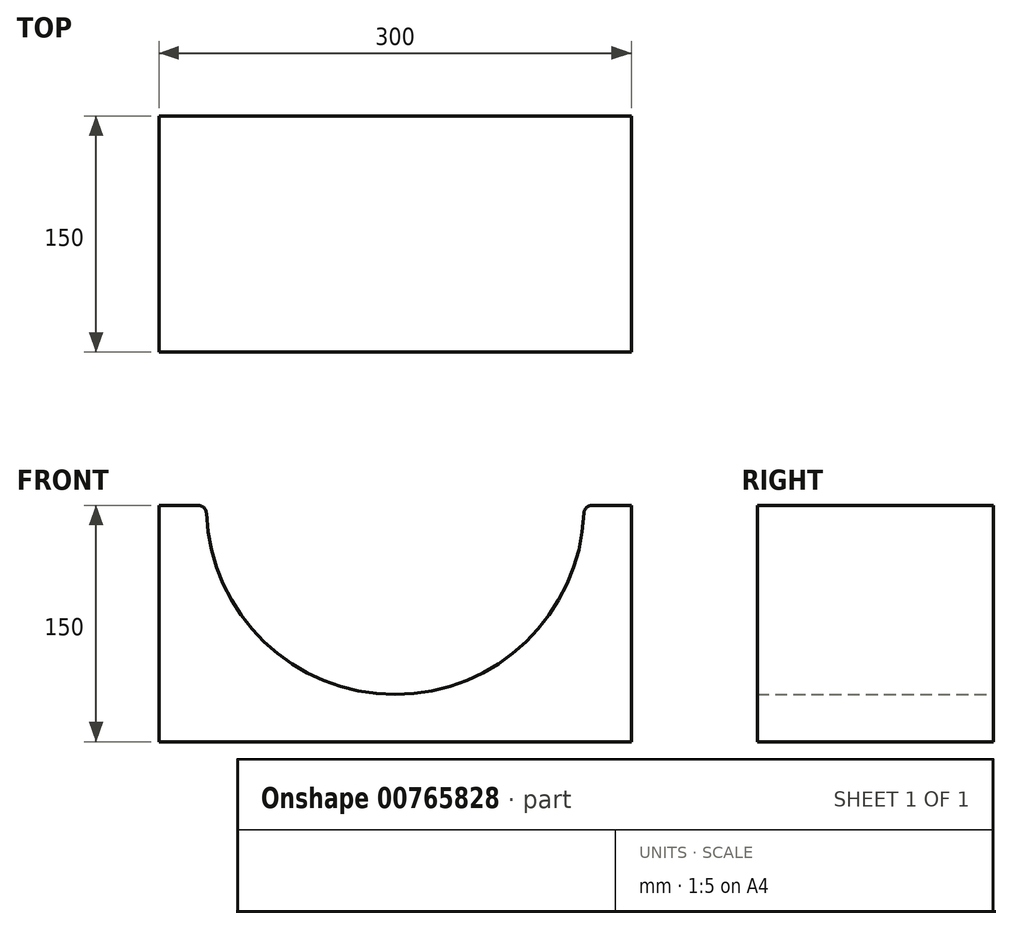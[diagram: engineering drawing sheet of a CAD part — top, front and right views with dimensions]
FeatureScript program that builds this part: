
annotation { "Feature Type Name" : "Feature", "Feature Type Description" : "" }
export const myFeature = defineFeature(function(context is Context, id is Id, definition is map)
    precondition{}
    {
        {
            var Q0;
            Q0=qCreatedBy(makeId("Front.planeOp"),FACE);
            var sketch = newSketch(context, id + "F0", { "sketchPlane" : qUnion([Q0])});
            skLineSegment(sketch, "E0", {"start": v(-35.62, 0) * mm, "end": v(-65.62, 0) * mm});
            skLineSegment(sketch, "E1", {"start": v(-65.62, 0) * mm, "end": v(-65.62, -150) * mm});
            skLineSegment(sketch, "E2", {"start": v(204.38, 0) * mm, "end": v(234.38, 0) * mm});
            skLineSegment(sketch, "E3", {"start": v(234.38, 0) * mm, "end": v(234.38, -150) * mm});
            skLineSegment(sketch, "E4", {"start": v(234.38, -150) * mm, "end": v(-65.62, -150) * mm});
            skArc(sketch, "E5", {"start": v(-35.62, 0) * mm, "mid": v(84.38, -120) * mm, "end": v(204.38, 0) * mm});
            skSolve(sketch);
        }
        {
            var Q0;
            Q0 = qSketchRegion(id + "F0", true);
            extrude(context, id + "F1", {"entities" : qUnion([Q0]), "depth" : 150 * mm, "offsetDistance" : 25 * mm});
        }
        {
            var Q0;
            Q0=makeQuery(id+"F1.opExtrude","SWEPT_EDGE",EDGE,{"disambiguationData":[OSD([sQuery(id+"F0.wireOp",EDGE,"E0"),sQuery(id+"F0.wireOp",EDGE,"E5")])]});
            var Q1;
            Q1=makeQuery(id+"F1.opExtrude","SWEPT_EDGE",EDGE,{"disambiguationData":[OSD([sQuery(id+"F0.wireOp",EDGE,"E2"),sQuery(id+"F0.wireOp",EDGE,"E5")])]});
            fillet(context, id + "F2", {"entities" : qUnion([Q0, Q1]), "radius" : 5 * mm, "tangentPropagation" : true, "allowEdgeOverflow" : false});
        }
    });
